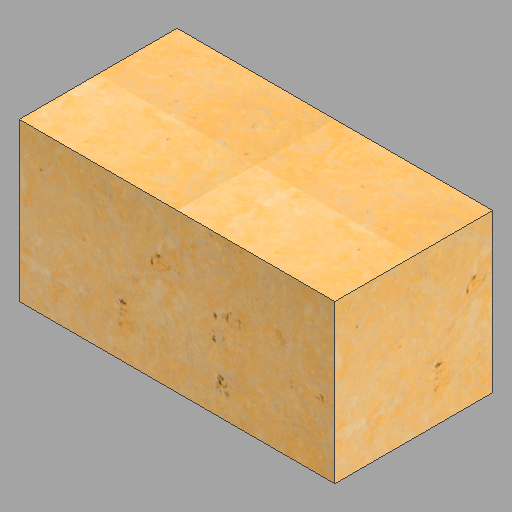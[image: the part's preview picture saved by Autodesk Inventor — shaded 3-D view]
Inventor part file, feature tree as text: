
AUTODESK INVENTOR PART (.ipt)
format: ipt  version: 2023 (Build 270158000, 158)  size: 398,336 bytes
history: native  units: in
note: dims shown in document units (in); Inventor stores cm internally (conversion verified against a paired STEP export)
features: extrude x1, sketch x1
ambient origin geometry x8: Origin, YZ Plane, XZ Plane, XY Plane, X Axis, Y Axis, Z Axis, Center Point
bodies: Solid1 (feature_tree)
feature tree (2):
  extrude  "Extrusion1"  Depth=24.0in
  sketch  "Sketch1"  dims[d0=48.0in d1=24.0in d2=24.0in d3=0.0in]
